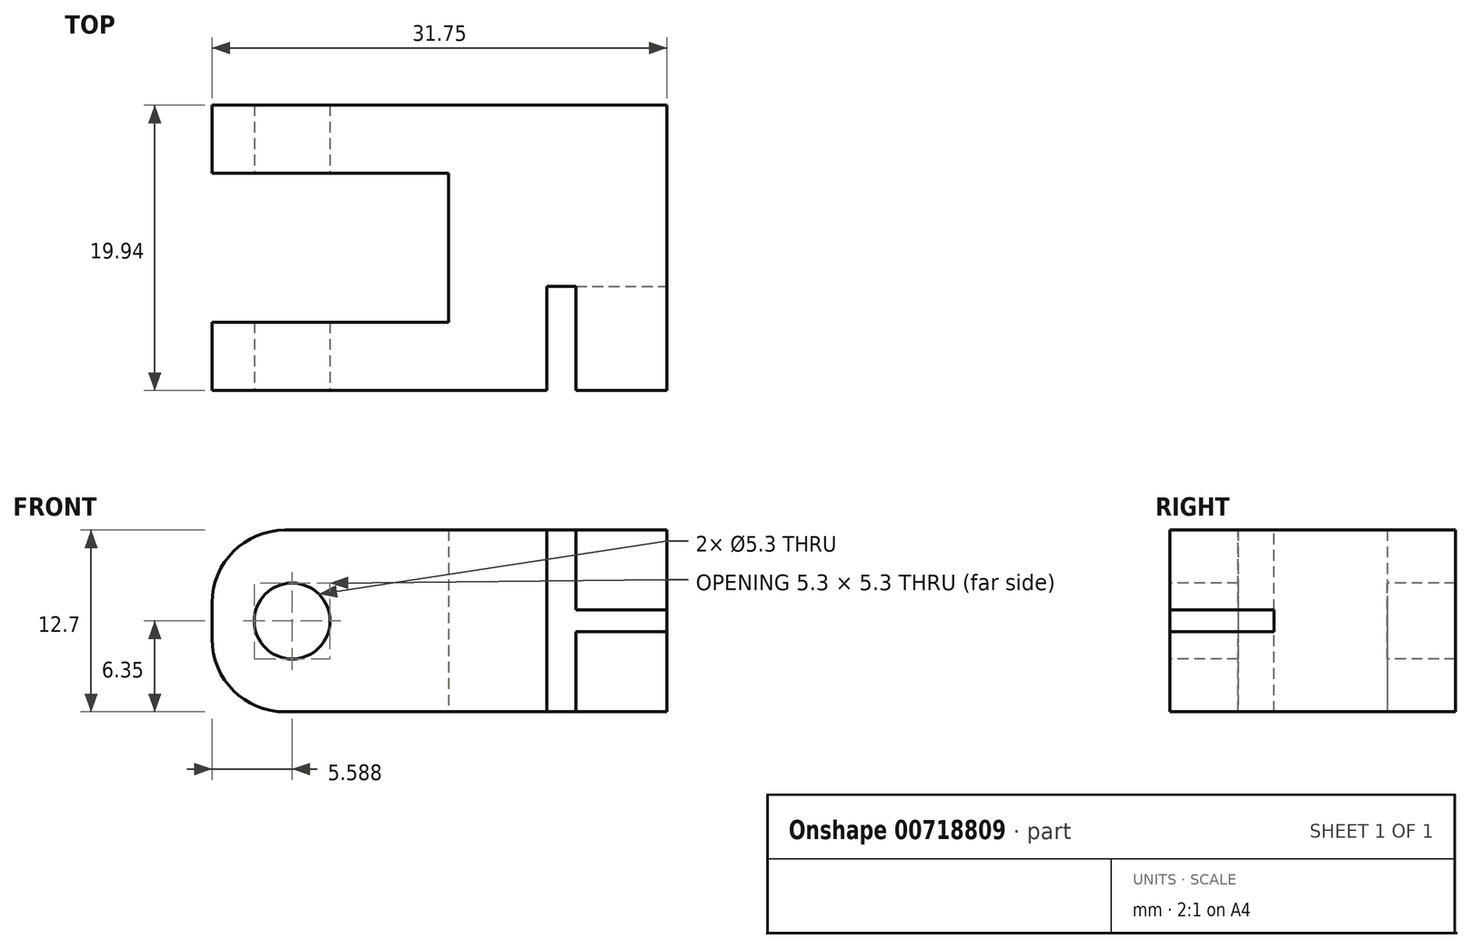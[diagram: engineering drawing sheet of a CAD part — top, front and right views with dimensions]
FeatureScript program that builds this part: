
annotation { "Feature Type Name" : "Feature", "Feature Type Description" : "" }
export const myFeature = defineFeature(function(context is Context, id is Id, definition is map)
    precondition{}
    {
        {
            var Q0;
            Q0=qCreatedBy(makeId("Top.planeOp"),FACE);
            var sketch = newSketch(context, id + "F0", { "sketchPlane" : qUnion([Q0])});
            skLineSegment(sketch, "E0", {"start": v(0, 0) * mm, "end": v(0, -4.76) * mm});
            skLineSegment(sketch, "E1", {"start": v(0, -4.76) * mm, "end": v(25.4, -4.76) * mm});
            skLineSegment(sketch, "E2", {"start": v(0, 0) * mm, "end": v(16.51, 0) * mm});
            skLineSegment(sketch, "E3", {"start": v(16.51, 0) * mm, "end": v(16.51, 10.41) * mm});
            skLineSegment(sketch, "E4", {"start": v(16.51, 10.41) * mm, "end": v(0, 10.41) * mm});
            skLineSegment(sketch, "E5", {"start": v(0, 10.41) * mm, "end": v(0, 15.18) * mm});
            skLineSegment(sketch, "E6", {"start": v(0, 15.18) * mm, "end": v(31.75, 15.18) * mm});
            skLineSegment(sketch, "E7", {"start": v(25.4, -4.76) * mm, "end": v(31.75, -4.76) * mm});
            skLineSegment(sketch, "E8", {"start": v(31.75, -4.76) * mm, "end": v(31.75, 15.18) * mm});
            skSolve(sketch);
        }
        {
            var Q0;
            Q0 = qSketchRegion(id + "F0", true);
            extrude(context, id + "F1", {"entities" : qUnion([Q0]), "depth" : 12.7 * mm, "offsetDistance" : 25.4 * mm});
        }
        {
            var Q0;
            Q0=makeQuery(id+"F1.opExtrude","SWEPT_FACE",FACE,{"disambiguationData":[OSD([sQuery(id+"F0.wireOp",EDGE,"E1"),sQuery(id+"F0.wireOp",EDGE,"E7")])]});
            var sketch = newSketch(context, id + "F2", { "sketchPlane" : qUnion([Q0])});
            skCircle(sketch, "E9", {"center": v(5.59, 6.35) * mm, "radius": 2.65 * mm});
            skSolve(sketch);
        }
        {
            var Q0;
            Q0 = qSketchRegion(id + "F2", true);
            extrude(context, id + "F3", {"entities" : qUnion([Q0]), "operationType" : NewBodyOperationType.REMOVE, "oppositeDirection" : true, "depth" : 51.82 * mm, "offsetDistance" : 25.4 * mm});
        }
        {
            var Q0;
            Q0=makeQuery(id+"F1.opExtrude","CAP_EDGE",EDGE,{"disambiguationData":[OSD([sQuery(id+"F0.wireOp",EDGE,"E0")])],"isStart":false});
            var Q1;
            Q1=makeQuery(id+"F1.opExtrude","CAP_EDGE",EDGE,{"disambiguationData":[OSD([sQuery(id+"F0.wireOp",EDGE,"E5")])],"isStart":false});
            var Q2;
            Q2=makeQuery(id+"F1.opExtrude","CAP_EDGE",EDGE,{"disambiguationData":[OSD([sQuery(id+"F0.wireOp",EDGE,"E0")])],"isStart":true});
            var Q3;
            Q3=makeQuery(id+"F1.opExtrude","CAP_EDGE",EDGE,{"disambiguationData":[OSD([sQuery(id+"F0.wireOp",EDGE,"E5")])],"isStart":true});
            fillet(context, id + "F4", {"entities" : qUnion([Q0, Q1, Q2, Q3]), "radius" : 5.08 * mm, "tangentPropagation" : true, "allowEdgeOverflow" : false});
        }
        {
            var Q0;
            Q0=makeQuery(id+"F1.opExtrude","SWEPT_FACE",FACE,{"disambiguationData":[OSD([sQuery(id+"F0.wireOp",EDGE,"E1"),sQuery(id+"F0.wireOp",EDGE,"E7")])]});
            var sketch = newSketch(context, id + "F5", { "sketchPlane" : qUnion([Q0])});
            skLineSegment(sketch, "E10", {"start": v(25.4, 14.79) * mm, "end": v(25.4, -2.13) * mm});
            skLineSegment(sketch, "E11", {"start": v(25.4, -2.13) * mm, "end": v(23.37, -2.13) * mm});
            skLineSegment(sketch, "E12", {"start": v(23.37, -2.13) * mm, "end": v(23.37, 14.79) * mm});
            skLineSegment(sketch, "E13", {"start": v(23.37, 14.79) * mm, "end": v(25.4, 14.79) * mm});
            skPoint(sketch, "E14.end.orphan", {"position": v(34.38, -2.13) * mm});
            skPoint(sketch, "E15.start.orphan", {"position": v(31.75, 6.35) * mm});
            skLineSegment(sketch, "E16", {"start": v(31.75, 6.35) * mm, "end": v(13.69, 6.35) * mm, "construction": true});
            skLineSegment(sketch, "E17", {"start": v(25.4, 5.59) * mm, "end": v(31.75, 5.59) * mm});
            skLineSegment(sketch, "E18.MirrorCS", {"start": v(25.4, 7.11) * mm, "end": v(31.75, 7.11) * mm});
            skSolve(sketch);
        }
        {
            var Q0;
            Q0 = qSketchRegion(id + "F5", true);
            var Q1;
            {var subQ0=sQuery(id+"F5.wireOp",EDGE,"E17");Q1=makeQuery(id+"F5.imprint","IMPRINT",FACE,{"disambiguationData":[TD([[makeQuery(id+"F5.imprint","IMPRINT",EDGE,{"derivedFrom":subQ0}),1.0]])]});}
            extrude(context, id + "F6", {"entities" : qUnion([Q0, Q1]), "operationType" : NewBodyOperationType.REMOVE, "oppositeDirection" : true, "depth" : 7.3 * mm, "offsetDistance" : 25.4 * mm});
        }
    });
